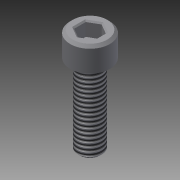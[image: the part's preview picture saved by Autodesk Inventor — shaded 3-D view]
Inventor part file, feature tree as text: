
AUTODESK INVENTOR PART (.ipt)
format: ipt  version: 2014 SP1 (Build 180222100, 222)  size: 99,328 bytes
history: native  units: in
note: dims shown in document units (in); Inventor stores cm internally (conversion verified against a paired STEP export)
features: other x2, thread x2, imported_body x1
ambient origin geometry x8: Origin, YZ Plane, XZ Plane, XY Plane, X Axis, Y Axis, Z Axis, Center Point
bodies: Body1 (feature_tree)
feature tree (5):
  other  "10-32x0625_shcs"
  other  "10-32x0625_shcs.ipt1"
  thread  "Thread1"  [1 undecoded]
  thread  "Thread2"  [1 undecoded]
  imported_body  "Base1"
note: 2 required parameter values undecoded (feature->parameter linkage not recoverable at this tier; creation-order binding heuristic only, values carry confidence <= 0.55)
